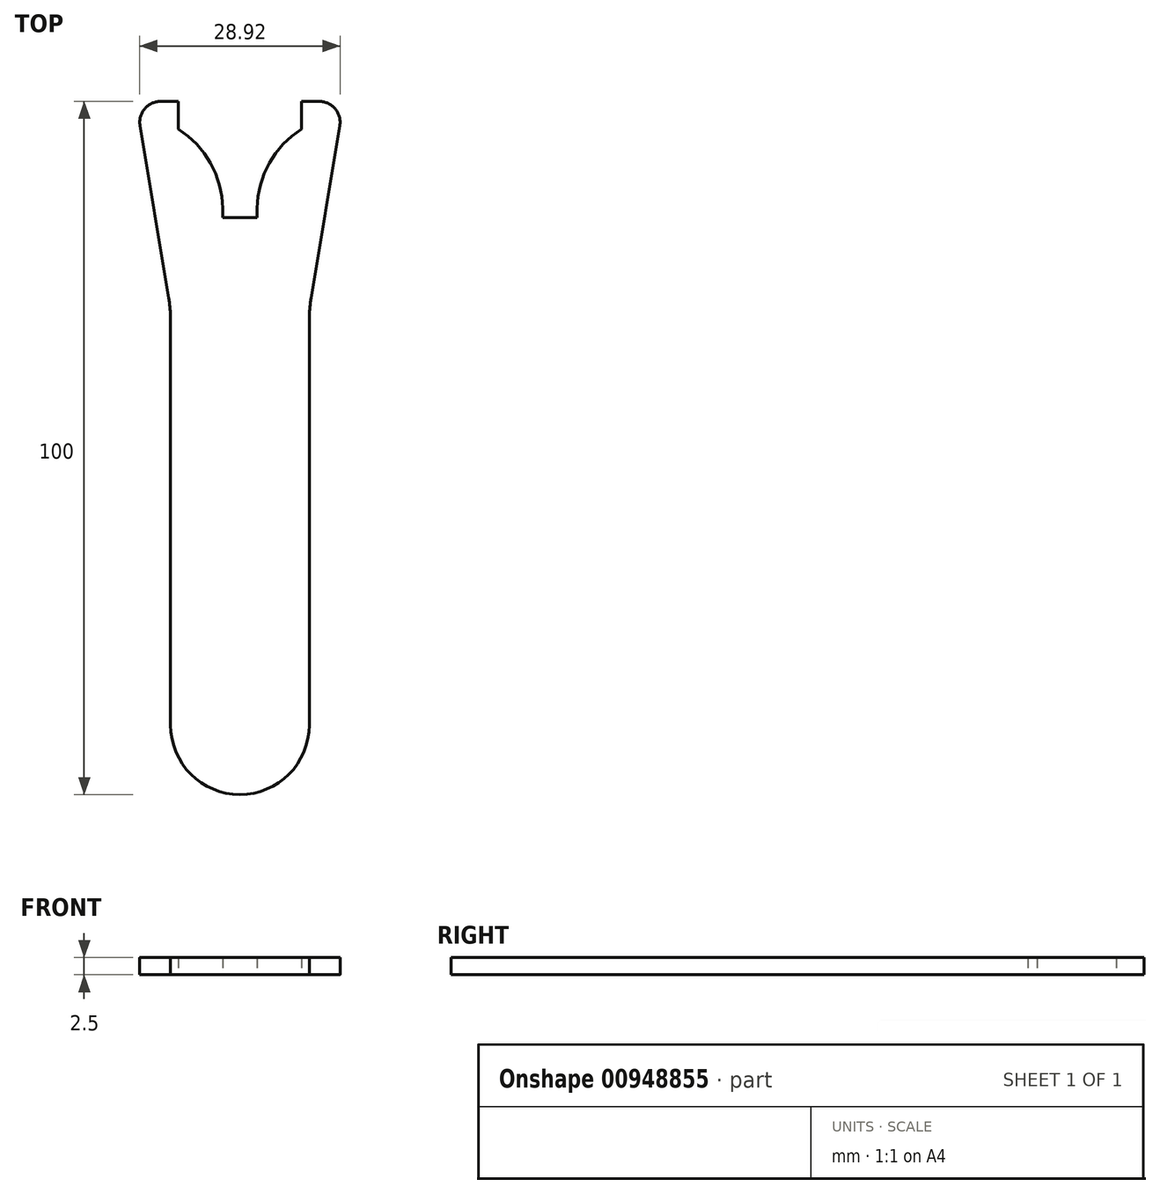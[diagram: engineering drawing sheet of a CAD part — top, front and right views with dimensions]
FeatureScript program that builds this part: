
annotation { "Feature Type Name" : "Feature", "Feature Type Description" : "" }
export const myFeature = defineFeature(function(context is Context, id is Id, definition is map)
    precondition{}
    {
        {
            var Q0;
            Q0=qCreatedBy(makeId("Top.planeOp"),FACE);
            var sketch = newSketch(context, id + "F0", { "sketchPlane" : qUnion([Q0])});
            skLineSegment(sketch, "E0", {"start": v(-2, -8.77) * mm, "end": v(2, -8.77) * mm, "construction": true});
            skLineSegment(sketch, "E1", {"start": v(0, -8.77) * mm, "end": v(0, 0) * mm, "construction": true});
            skPoint(sketch, "E1.startSnap0", {"position": v(0, -8.77) * mm});
            skArc(sketch, "E2", {"start": v(8.6, 2.66) * mm, "mid": v(3.9, -2.25) * mm, "end": v(2, -8.77) * mm});
            skArc(sketch, "E3.MirrorC", {"start": v(-8.6, 2.66) * mm, "mid": v(-3.9, -2.25) * mm, "end": v(-2, -8.77) * mm});
            skArc(sketch, "E4", {"start": v(-2, -8.77) * mm, "mid": v(0, -9) * mm, "end": v(2, -8.77) * mm});
            skCircle(sketch, "E5", {"center": v(0, 0) * mm, "radius": 4.5 * mm, "construction": true});
            skLineSegment(sketch, "E6", {"start": v(-16.24, -9.38) * mm, "end": v(0, 0) * mm, "construction": true});
            skLineSegment(sketch, "E7", {"start": v(0, 0) * mm, "end": v(0, 18.76) * mm, "construction": true});
            skArc(sketch, "E8", {"start": v(-6.6, 6.12) * mm, "mid": v(0, 4.5) * mm, "end": v(6.6, 6.12) * mm});
            skPoint(sketch, "E9", {"position": v(-8.6, 2.66) * mm});
            skPoint(sketch, "E10", {"position": v(-6.6, 6.12) * mm});
            skLineSegment(sketch, "E11", {"start": v(-8.6, 2.66) * mm, "end": v(-6.6, 6.12) * mm, "construction": true});
            skArc(sketch, "E12.trimOffspring", {"start": v(8.6, 2.66) * mm, "mid": v(7.8, 4.5) * mm, "end": v(6.6, 6.12) * mm});
            skArc(sketch, "E13.trimOffspring", {"start": v(-6.6, 6.12) * mm, "mid": v(-7.8, 4.5) * mm, "end": v(-8.6, 2.66) * mm});
            skSolve(sketch);
        }
        {
            var Q0;
            Q0=qCreatedBy(makeId("Top.planeOp"),FACE);
            var sketch = newSketch(context, id + "F1", { "sketchPlane" : qUnion([Q0])});
            skArc(sketch, "E14.0", {"start": v(-8.6, 2.66) * mm, "mid": v(-3.9, -2.25) * mm, "end": v(-2, -8.77) * mm, "construction": true});
            skArc(sketch, "E15.0", {"start": v(8.6, 2.66) * mm, "mid": v(3.9, -2.25) * mm, "end": v(2, -8.77) * mm, "construction": true});
            skLineSegment(sketch, "E16", {"start": v(-2.49, -10.5) * mm, "end": v(2.49, -10.5) * mm});
            skLineSegment(sketch, "E17", {"start": v(-8.9, 6.25) * mm, "end": v(-15, 6.25) * mm});
            skLineSegment(sketch, "E18", {"start": v(-15, 6.25) * mm, "end": v(-10, -23.75) * mm});
            skLineSegment(sketch, "E19", {"start": v(-10, -23.75) * mm, "end": v(-10, -83.75) * mm});
            skLineSegment(sketch, "E20", {"start": v(0, 0) * mm, "end": v(0, -83.75) * mm, "construction": true});
            skLineSegment(sketch, "E21.MirrorCS", {"start": v(8.9, 6.25) * mm, "end": v(15, 6.25) * mm});
            skLineSegment(sketch, "E22.MirrorCS", {"start": v(10, -23.75) * mm, "end": v(10, -83.75) * mm});
            skLineSegment(sketch, "E23.MirrorCS", {"start": v(15, 6.25) * mm, "end": v(10, -23.75) * mm});
            skArc(sketch, "E24", {"start": v(-10, -83.75) * mm, "mid": v(0, -93.75) * mm, "end": v(10, -83.75) * mm});
            skArc(sketch, "E25.0", {"start": v(-8.9, 2.25) * mm, "mid": v(-4.25, -2.65) * mm, "end": v(-2.49, -9.17) * mm});
            skArc(sketch, "E25.1", {"start": v(-2.49, -9.17) * mm, "mid": v(0, -9.5) * mm, "end": v(2.49, -9.17) * mm, "construction": true});
            skArc(sketch, "E25.2", {"start": v(8.9, 2.25) * mm, "mid": v(4.25, -2.65) * mm, "end": v(2.49, -9.17) * mm});
            skLineSegment(sketch, "E26", {"start": v(-2.49, -9.17) * mm, "end": v(-2.49, -10.5) * mm});
            skLineSegment(sketch, "E27", {"start": v(2.49, -9.17) * mm, "end": v(2.49, -10.5) * mm});
            skLineSegment(sketch, "E28", {"start": v(-8.9, 2.25) * mm, "end": v(-8.9, 6.25) * mm});
            skLineSegment(sketch, "E29", {"start": v(8.9, 2.25) * mm, "end": v(8.9, 6.25) * mm});
            skPoint(sketch, "E30.MirrorCS.start.orphan", {"position": v(8.6, 2.66) * mm});
            skSolve(sketch);
        }
        {
            var Q0;
            Q0 = qSketchRegion(id + "F1", true);
            extrude(context, id + "F2", {"entities" : qUnion([Q0]), "depth" : 2.5 * mm, "offsetDistance" : 25 * mm});
        }
        {
            var Q0;
            Q0=makeQuery(id+"F2.opExtrude","SWEPT_EDGE",EDGE,{"disambiguationData":[OSD([sQuery(id+"F1.wireOp",EDGE,"E17"),sQuery(id+"F1.wireOp",EDGE,"E18")])]});
            var Q1;
            Q1=makeQuery(id+"F2.opExtrude","SWEPT_EDGE",EDGE,{"disambiguationData":[OSD([sQuery(id+"F1.wireOp",EDGE,"E21.MirrorCS"),sQuery(id+"F1.wireOp",EDGE,"E23.MirrorCS")])]});
            fillet(context, id + "F3", {"entities" : qUnion([Q0, Q1]), "radius" : 3 * mm, "tangentPropagation" : true, "allowEdgeOverflow" : false});
        }
        {
            var Q0;
            Q0=makeQuery(id+"F2.opExtrude","SWEPT_EDGE",EDGE,{"disambiguationData":[OSD([sQuery(id+"F1.wireOp",EDGE,"E18"),sQuery(id+"F1.wireOp",EDGE,"E19")])]});
            var Q1;
            Q1=makeQuery(id+"F2.opExtrude","SWEPT_EDGE",EDGE,{"disambiguationData":[OSD([sQuery(id+"F1.wireOp",EDGE,"E22.MirrorCS"),sQuery(id+"F1.wireOp",EDGE,"E23.MirrorCS")])]});
            fillet(context, id + "F4", {"entities" : qUnion([Q0, Q1]), "radius" : 20 * mm, "tangentPropagation" : true, "allowEdgeOverflow" : false});
        }
    });
